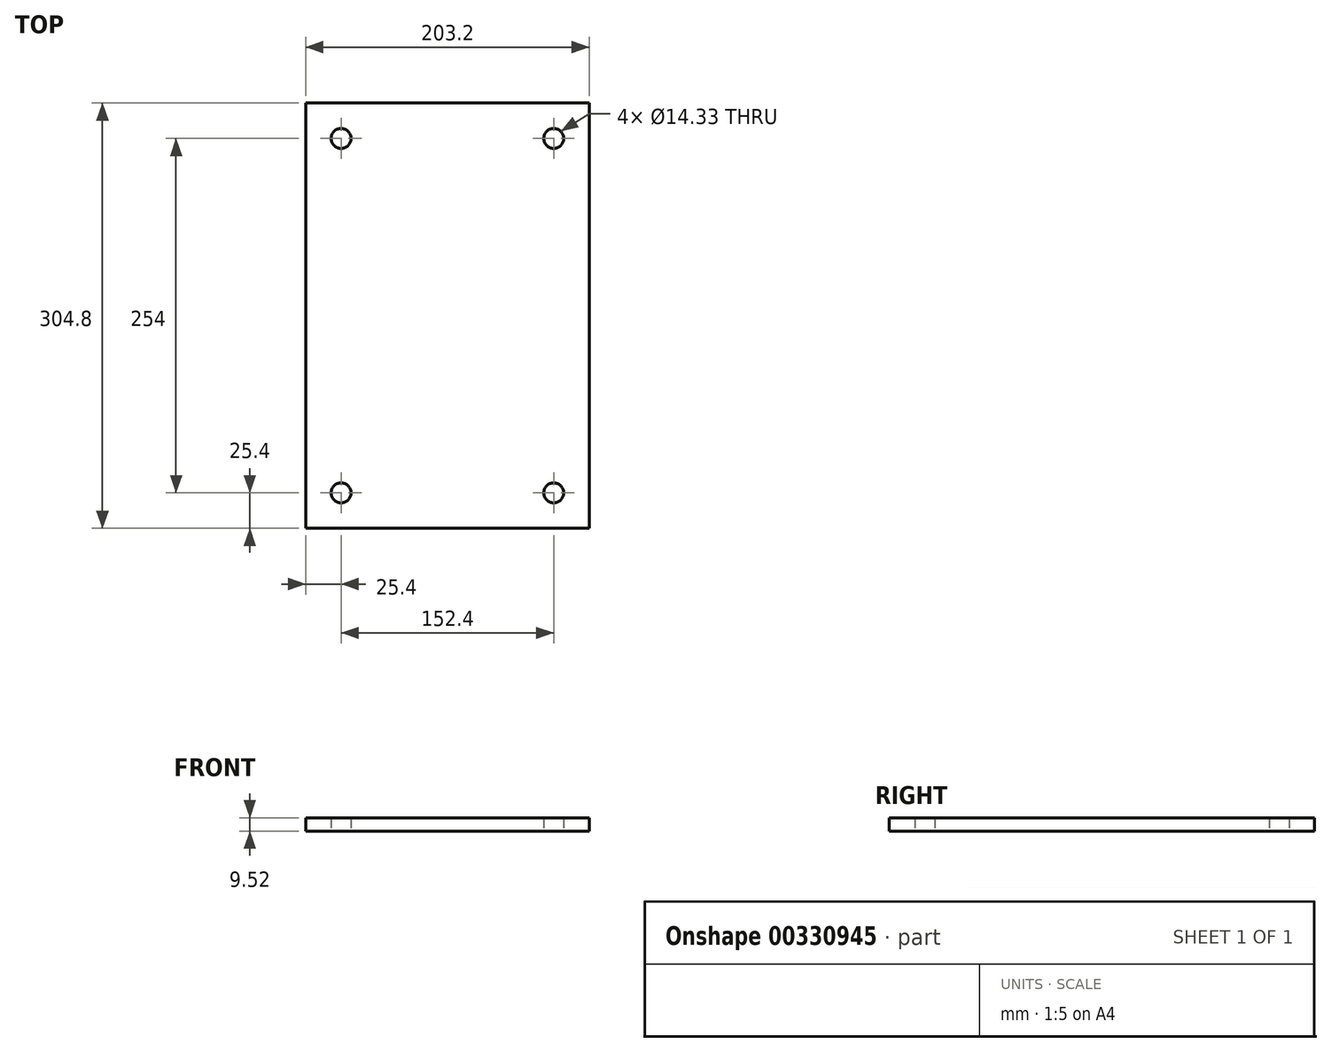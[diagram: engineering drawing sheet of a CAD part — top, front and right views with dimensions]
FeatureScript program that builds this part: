
annotation { "Feature Type Name" : "Feature", "Feature Type Description" : "" }
export const myFeature = defineFeature(function(context is Context, id is Id, definition is map)
    precondition{}
    {
        {
            var Q0;
            Q0=qCreatedBy(makeId("Top.planeOp"),FACE);
            var sketch = newSketch(context, id + "F0", { "sketchPlane" : qUnion([Q0])});
            skLineSegment(sketch, "E0.bottom", {"start": v(101.6, -152.4) * mm, "end": v(-101.6, -152.4) * mm});
            skLineSegment(sketch, "E0.top", {"start": v(101.6, 152.4) * mm, "end": v(-101.6, 152.4) * mm});
            skLineSegment(sketch, "E0.left", {"start": v(101.6, -152.4) * mm, "end": v(101.6, 152.4) * mm});
            skLineSegment(sketch, "E0.right", {"start": v(-101.6, -152.4) * mm, "end": v(-101.6, 152.4) * mm});
            skPoint(sketch, "E0.middle", {"position": v(0, 0) * mm});
            skCircle(sketch, "E1", {"center": v(-76.2, 127) * mm, "radius": 7.16 * mm});
            skCircle(sketch, "E2", {"center": v(76.2, 127) * mm, "radius": 7.16 * mm});
            skCircle(sketch, "E3", {"center": v(-76.2, -127) * mm, "radius": 7.16 * mm});
            skCircle(sketch, "E4", {"center": v(76.2, -127) * mm, "radius": 7.16 * mm});
            skSolve(sketch);
        }
        {
            var Q0;
            Q0=makeQuery(id+"F0.imprint","IMPRINT",FACE,{"disambiguationData":[TD([[makeQuery(id+"F0.imprint","IMPRINT",EDGE,{"derivedFrom":sQuery(id+"F0.wireOp",EDGE,"E0.bottom")}),-1.0]])]});
            extrude(context, id + "F1", {"entities" : qUnion([Q0]), "endBound" : BoundingType.SYMMETRIC, "depth" : 9.52 * mm});
        }
    });
